FCSTD DOCUMENT  (FreeCAD 0.17R13522 (Git))
Label: bed
License: CreativeCommons Attribution-ShareAlike
LicenseURL: http://creativecommons.org/licenses/by-sa/4.0/
objects: Sketcher::SketchObject×3, PartDesign::Body×3, Part::FeaturePython×2
note: 8 computed .brp shape members not serialized (recipe doc carries the construction recipe); baked Part::Feature solids carry a one-line shape summary decoded from their .brp

FEATURE [Sketcher::SketchObject] Sketch  label="grid-line-vertical"
  MapMode = 5
  Support = -> [XY_Plane]
  sketch-geometry (1):
    g0: LineSegment StartX=0 StartY=150 StartZ=0 EndX=0 EndY=0 EndZ=0
  constraints (3):
    c: PointOnObject(g0,g-2)
    c: Coincident(g0,g-1)
    c: DistanceY(g0,g0) = 150
FEATURE [PartDesign::Body] Body
  Group = -> [Sketch]
  Origin = -> Origin
FEATURE [Sketcher::SketchObject] Sketch001  label="grid-line-horizontal"
  MapMode = 5
  Support = -> [XY_Plane001]
  sketch-geometry (1):
    g0: LineSegment StartX=0 StartY=0 StartZ=0 EndX=250 EndY=0 EndZ=0
  constraints (3):
    c: Coincident(g0,g-1)
    c: Horizontal(g0)
    c: DistanceX(g0,g0) = 250
FEATURE [PartDesign::Body] Body001
  Group = -> [Sketch001]
  Origin = -> Origin001
FEATURE [Part::FeaturePython] Array  # Draft array (typed FeaturePython)
  Angle = 360
  ArrayType = 0
  Axis = (0,0,1)
  Base = -> Sketch001
  Center = (0,0,0)
  Fuse = false
  IntervalAxis = (0,0,0)
  IntervalX = (1,0,0)
  IntervalY = (0,10,0)
  IntervalZ = (0,0,0)
  NumberPolar = 1
  NumberX = 1
  NumberY = 15
  NumberZ = 1
FEATURE [Part::FeaturePython] Array001  # Draft array (typed FeaturePython)
  Angle = 360
  ArrayType = 0
  Axis = (0,0,1)
  Base = -> Sketch
  Center = (0,0,0)
  Fuse = false
  IntervalAxis = (0,0,0)
  IntervalX = (10,0,0)
  IntervalY = (0,1,0)
  IntervalZ = (0,0,0)
  NumberPolar = 1
  NumberX = 25
  NumberY = 1
  NumberZ = 1
FEATURE [Sketcher::SketchObject] Sketch002  label="surfacing"
  MapMode = 5
  Support = -> [XY_Plane002]
  sketch-geometry (4):
    g0: LineSegment StartX=0 StartY=0 StartZ=0 EndX=260 EndY=0 EndZ=0
    g1: LineSegment StartX=260 StartY=0 StartZ=0 EndX=260 EndY=160 EndZ=0
    g2: LineSegment StartX=260 StartY=160 StartZ=0 EndX=0 EndY=160 EndZ=0
    g3: LineSegment StartX=0 StartY=160 StartZ=0 EndX=0 EndY=0 EndZ=0
  constraints (11):
    c: Coincident(g0,g1)
    c: Coincident(g1,g2)
    c: Coincident(g2,g3)
    c: Coincident(g3,g0)
    c: Horizontal(g0)
    c: Horizontal(g2)
    c: Vertical(g1)
    c: Vertical(g3)
    c: Coincident(g0,g-1)
    c: DistanceY(g1) = 160
    c: DistanceX(g0,g0) = 260
FEATURE [PartDesign::Body] Body002
  Group = -> [Sketch002]
  Origin = -> Origin002
  Placement = pos=(-5,-5,0) rot=(0,0,1;0rad)
